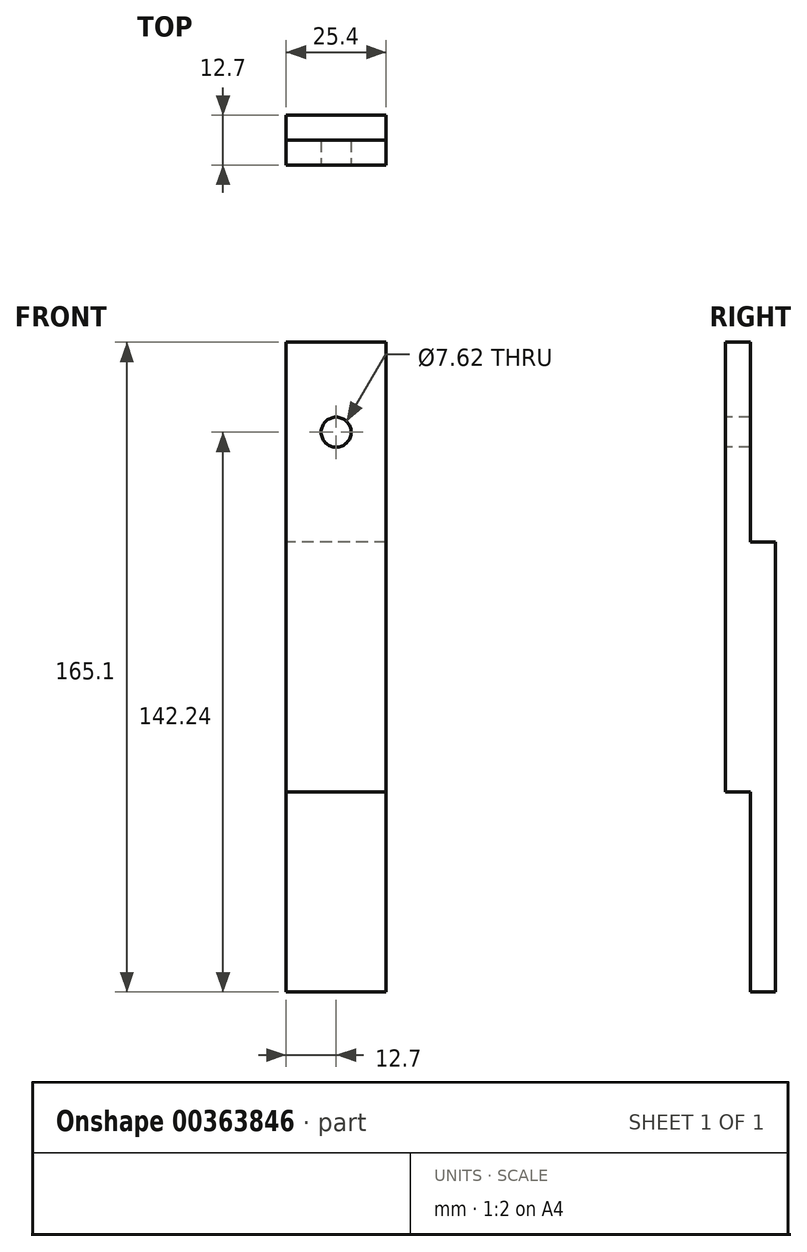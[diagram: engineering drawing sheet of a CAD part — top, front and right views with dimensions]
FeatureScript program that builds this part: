
annotation { "Feature Type Name" : "Feature", "Feature Type Description" : "" }
export const myFeature = defineFeature(function(context is Context, id is Id, definition is map)
    precondition{}
    {
        {
            var Q0;
            Q0=qCreatedBy(makeId("Front.planeOp"),FACE);
            var sketch = newSketch(context, id + "F0", { "sketchPlane" : qUnion([Q0])});
            skLineSegment(sketch, "E0.bottom", {"start": v(0, 0) * mm, "end": v(25.4, 0) * mm});
            skLineSegment(sketch, "E0.top", {"start": v(0, 165.1) * mm, "end": v(25.4, 165.1) * mm});
            skLineSegment(sketch, "E0.left", {"start": v(0, 0) * mm, "end": v(0, 165.1) * mm});
            skLineSegment(sketch, "E0.right", {"start": v(25.4, 0) * mm, "end": v(25.4, 165.1) * mm});
            skSolve(sketch);
        }
        {
            var Q0;
            Q0 = qSketchRegion(id + "F0", true);
            extrude(context, id + "F1", {"entities" : qUnion([Q0]), "depth" : 12.7 * mm});
        }
        {
            var Q0;
            Q0=makeQuery(id+"F1.opExtrude","CAP_FACE",FACE,{"disambiguationData":[OSD([sQuery(id+"F0.wireOp",EDGE,"E0.bottom"),sQuery(id+"F0.wireOp",EDGE,"E0.top"),sQuery(id+"F0.wireOp",EDGE,"E0.left"),sQuery(id+"F0.wireOp",EDGE,"E0.right")])],"isStart":false});
            var sketch = newSketch(context, id + "F2", { "sketchPlane" : qUnion([Q0])});
            skLineSegment(sketch, "E1.bottom", {"start": v(0, 0) * mm, "end": v(25.4, 0) * mm});
            skLineSegment(sketch, "E1.top", {"start": v(0, 50.8) * mm, "end": v(25.4, 50.8) * mm});
            skLineSegment(sketch, "E1.left", {"start": v(0, 0) * mm, "end": v(0, 50.8) * mm});
            skLineSegment(sketch, "E1.right", {"start": v(25.4, 0) * mm, "end": v(25.4, 50.8) * mm});
            skSolve(sketch);
        }
        {
            var Q0;
            Q0=makeQuery(id+"F2.imprint","IMPRINT",FACE,{"disambiguationData":[TD([[makeQuery(id+"F2.imprint","IMPRINT",EDGE,{"derivedFrom":sQuery(id+"F2.wireOp",EDGE,"E1.bottom")}),1.0]])]});
            extrude(context, id + "F3", {"entities" : qUnion([Q0]), "operationType" : NewBodyOperationType.ADD, "oppositeDirection" : true, "depth" : 6.35 * mm});
        }
        {
            var Q0;
            Q0 = qSketchRegion(id + "F2", true);
            extrude(context, id + "F4", {"entities" : qUnion([Q0]), "operationType" : NewBodyOperationType.REMOVE, "oppositeDirection" : true, "depth" : 6.35 * mm});
        }
        {
            var Q0;
            Q0=makeQuery(id+"F1.opExtrude","CAP_FACE",FACE,{"disambiguationData":[OSD([sQuery(id+"F0.wireOp",EDGE,"E0.bottom"),sQuery(id+"F0.wireOp",EDGE,"E0.top"),sQuery(id+"F0.wireOp",EDGE,"E0.left"),sQuery(id+"F0.wireOp",EDGE,"E0.right")])],"isStart":true});
            var sketch = newSketch(context, id + "F5", { "sketchPlane" : qUnion([Q0])});
            skLineSegment(sketch, "E2.bottom", {"start": v(-25.4, 165.1) * mm, "end": v(0, 165.1) * mm});
            skLineSegment(sketch, "E2.top", {"start": v(-25.4, 114.3) * mm, "end": v(0, 114.3) * mm});
            skLineSegment(sketch, "E2.left", {"start": v(-25.4, 165.1) * mm, "end": v(-25.4, 114.3) * mm});
            skLineSegment(sketch, "E2.right", {"start": v(0, 165.1) * mm, "end": v(0, 114.3) * mm});
            skSolve(sketch);
        }
        {
            var Q0;
            Q0=makeQuery(id+"F5.imprint","IMPRINT",FACE,{"disambiguationData":[TD([[makeQuery(id+"F5.imprint","IMPRINT",EDGE,{"derivedFrom":sQuery(id+"F5.wireOp",EDGE,"E2.bottom")}),1.0]])]});
            extrude(context, id + "F6", {"entities" : qUnion([Q0]), "operationType" : NewBodyOperationType.REMOVE, "oppositeDirection" : true, "depth" : 6.35 * mm});
        }
        {
            var Q0;
            Q0=makeQuery(id+"F1.opExtrude","CAP_FACE",FACE,{"disambiguationData":[OSD([sQuery(id+"F0.wireOp",EDGE,"E0.bottom"),sQuery(id+"F0.wireOp",EDGE,"E0.top"),sQuery(id+"F0.wireOp",EDGE,"E0.left"),sQuery(id+"F0.wireOp",EDGE,"E0.right")])],"isStart":false});
            var sketch = newSketch(context, id + "F7", { "sketchPlane" : qUnion([Q0])});
            skCircle(sketch, "E3", {"center": v(12.7, 142.24) * mm, "radius": 3.81 * mm});
            skSolve(sketch);
        }
        {
            var Q0;
            Q0=makeQuery(id+"F7.imprint","IMPRINT",FACE,{"disambiguationData":[TD([[makeQuery(id+"F7.imprint","IMPRINT",EDGE,{"derivedFrom":sQuery(id+"F7.wireOp",EDGE,"E3")}),1.0]])]});
            extrude(context, id + "F8", {"entities" : qUnion([Q0]), "operationType" : NewBodyOperationType.REMOVE, "oppositeDirection" : true, "depth" : 25.4 * mm});
        }
    });
